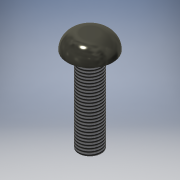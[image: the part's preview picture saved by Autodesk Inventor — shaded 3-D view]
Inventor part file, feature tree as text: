
AUTODESK INVENTOR PART (.ipt)
format: ipt  version: 2016 (Build 200138000, 138)  size: 139,264 bytes
history: native  units: mm
features: extrude x3, sketch x3, other x1, fillet x1, thread x1
ambient origin geometry x1: Origin
bodies: Body1 (feature_tree)
feature tree (9):
  other  "ソリッド1"
  extrude  "押し出し1"  Depth=4.0mm
  extrude  "押し出し2"  Depth=6.0mm TaperAngle=0.0deg
  fillet  "フィレット1"  Radius=8.0mm
  thread  "ねじ1"
  extrude  "押し出し3"  Depth=2.6mm TaperAngle=0.0deg
  sketch  "スケッチ1"
  sketch  "スケッチ2"
  sketch  "スケッチ3"
